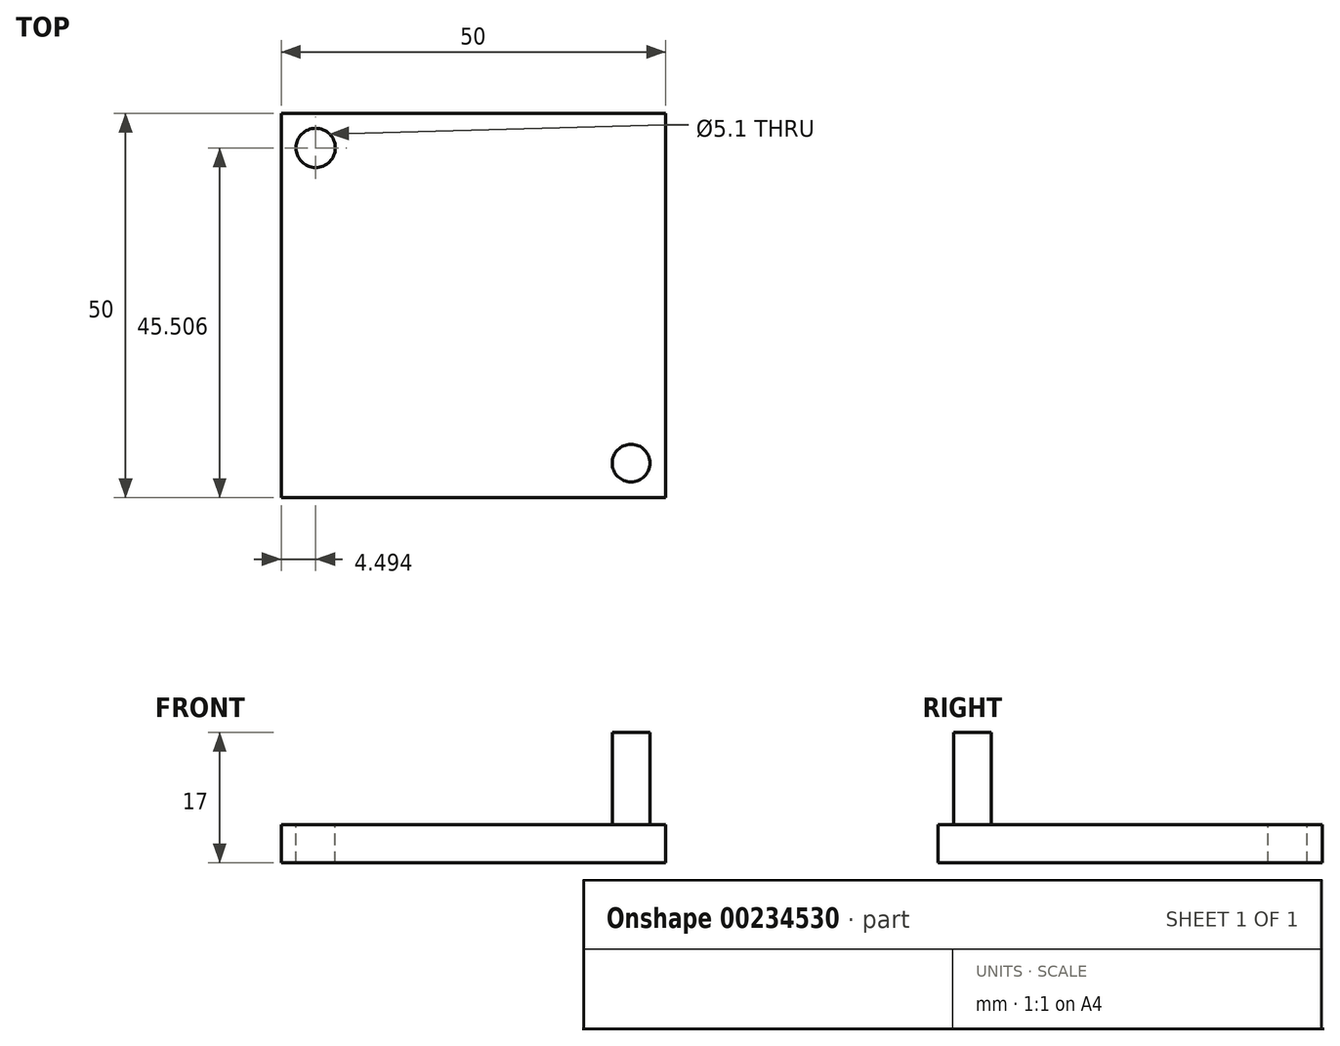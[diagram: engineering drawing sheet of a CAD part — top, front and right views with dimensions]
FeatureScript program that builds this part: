
annotation { "Feature Type Name" : "Feature", "Feature Type Description" : "" }
export const myFeature = defineFeature(function(context is Context, id is Id, definition is map)
    precondition{}
    {
        {
            var Q0;
            Q0=qCreatedBy(makeId("Top.planeOp"),FACE);
            var sketch = newSketch(context, id + "F0", { "sketchPlane" : qUnion([Q0])});
            skLineSegment(sketch, "E0.bottom", {"start": v(-25, 25) * mm, "end": v(25, 25) * mm});
            skLineSegment(sketch, "E0.top", {"start": v(-25, -25) * mm, "end": v(25, -25) * mm});
            skLineSegment(sketch, "E0.left", {"start": v(-25, 25) * mm, "end": v(-25, -25) * mm});
            skLineSegment(sketch, "E0.right", {"start": v(25, 25) * mm, "end": v(25, -25) * mm});
            skLineSegment(sketch, "E1", {"start": v(0, 0) * mm, "end": v(-25, 0) * mm});
            skLineSegment(sketch, "E2", {"start": v(0, 25) * mm, "end": v(0, 0) * mm});
            skSolve(sketch);
        }
        {
            var Q0;
            Q0=makeQuery(id+"F0.imprint","IMPRINT",FACE,{"disambiguationData":[TD([[makeQuery(id+"F0.imprint","IMPRINT",EDGE,{"derivedFrom":sQuery(id+"F0.wireOp",EDGE,"E0.bottom")}),-1.0]])]});
            var Q1;
            {var subQ2=sQuery(id+"F0.wireOp",EDGE,"E0.top");Q1=makeQuery(id+"F0.imprint","IMPRINT",FACE,{"disambiguationData":[TD([[makeQuery(id+"F0.imprint","IMPRINT",EDGE,{"derivedFrom":subQ2}),1.0]])]});}
            extrude(context, id + "F1", {"entities" : qUnion([Q0, Q1]), "depth" : 5 * mm});
        }
        {
            var Q0;
            Q0=makeQuery(id+"F1.opExtrude","CAP_FACE",FACE,{"disambiguationData":[OSD([sQuery(id+"F0.wireOp",EDGE,"E0.bottom"),sQuery(id+"F0.wireOp",EDGE,"E0.top"),sQuery(id+"F0.wireOp",EDGE,"E0.left"),sQuery(id+"F0.wireOp",EDGE,"E0.right")])],"isStart":false});
            var sketch = newSketch(context, id + "F2", { "sketchPlane" : qUnion([Q0])});
            skCircle(sketch, "E3", {"center": v(20.5, -20.5) * mm, "radius": 2.45 * mm});
            skCircle(sketch, "E4", {"center": v(-20.5, 20.5) * mm, "radius": 2.55 * mm});
            skLineSegment(sketch, "E5", {"start": v(-20.5, 20.5) * mm, "end": v(20.5, -20.5) * mm});
            skSolve(sketch);
        }
        {
            var Q0;
            Q0=makeQuery(id+"F2.imprint","IMPRINT",FACE,{"disambiguationData":[TD([[makeQuery(id+"F2.imprint","IMPRINT",EDGE,{"derivedFrom":sQuery(id+"F2.wireOp",EDGE,"E3")}),1.0]])]});
            extrude(context, id + "F3", {"entities" : qUnion([Q0]), "operationType" : NewBodyOperationType.ADD, "depth" : 12 * mm});
        }
        {
            var Q0;
            Q0=makeQuery(id+"F2.imprint","IMPRINT",FACE,{"disambiguationData":[TD([[makeQuery(id+"F2.imprint","IMPRINT",EDGE,{"derivedFrom":sQuery(id+"F2.wireOp",EDGE,"E4")}),1.0]])]});
            extrude(context, id + "F4", {"entities" : qUnion([Q0]), "operationType" : NewBodyOperationType.REMOVE, "endBound" : BoundingType.THROUGH_ALL, "oppositeDirection" : true, "depth" : 25 * mm});
        }
    });
